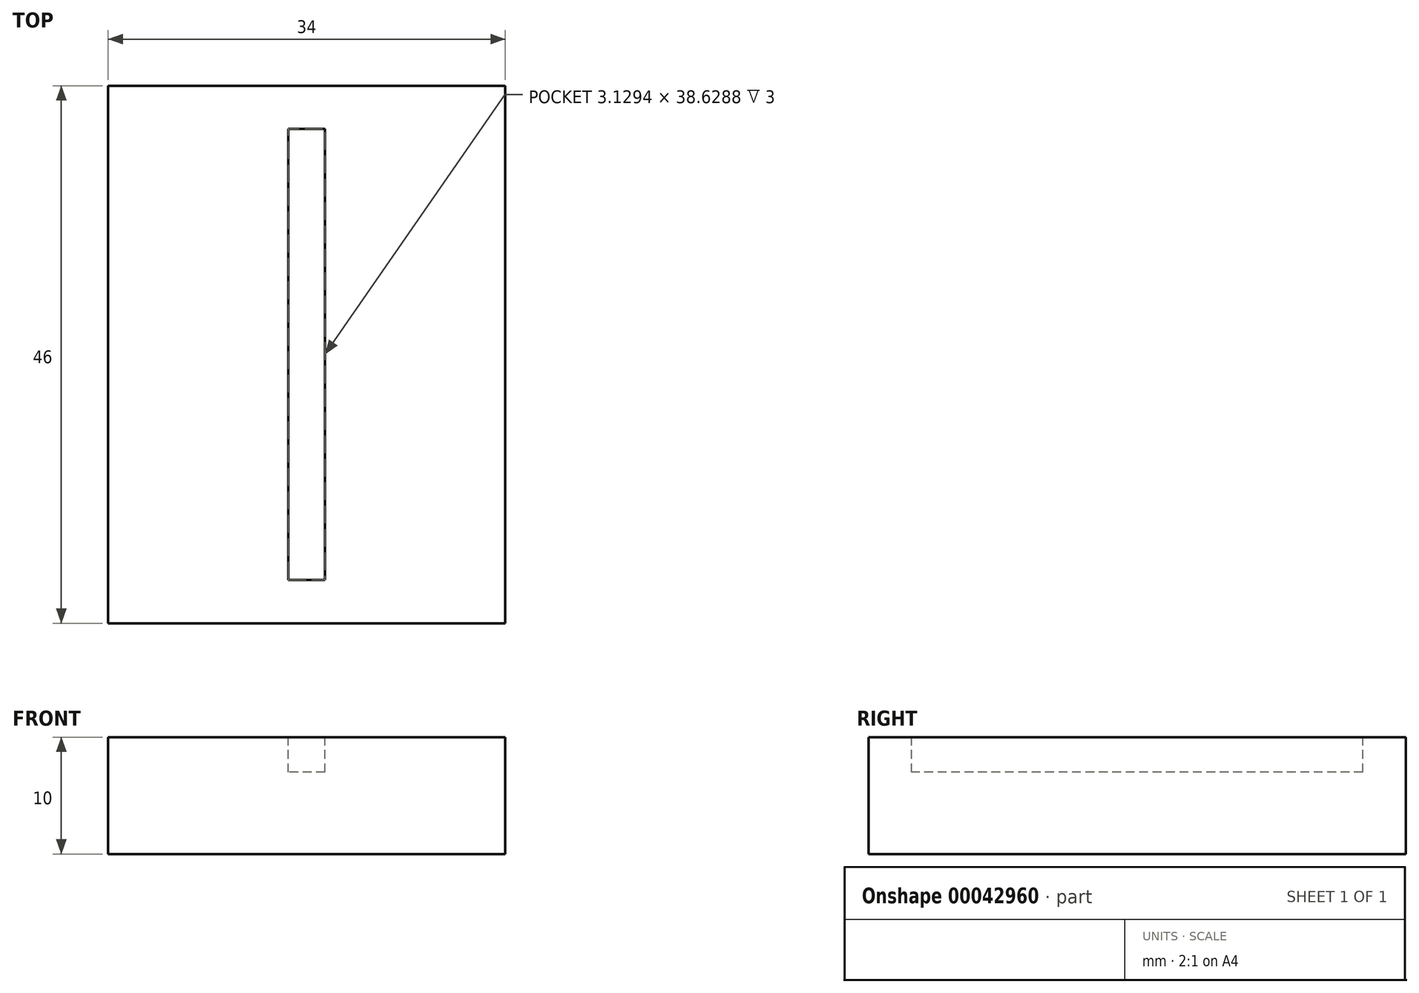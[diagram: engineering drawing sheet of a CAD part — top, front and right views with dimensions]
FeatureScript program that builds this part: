
annotation { "Feature Type Name" : "Feature", "Feature Type Description" : "" }
export const myFeature = defineFeature(function(context is Context, id is Id, definition is map)
    precondition{}
    {
        {
            var Q0;
            Q0=qCreatedBy(makeId("Top.planeOp"),FACE);
            var sketch = newSketch(context, id + "F0", { "sketchPlane" : qUnion([Q0])});
            skLineSegment(sketch, "E0.rect.bottom", {"start": v(17, 23) * mm, "end": v(-17, 23) * mm});
            skLineSegment(sketch, "E0.rect.top", {"start": v(17, -23) * mm, "end": v(-17, -23) * mm});
            skLineSegment(sketch, "E0.rect.left", {"start": v(17, 23) * mm, "end": v(17, -23) * mm});
            skLineSegment(sketch, "E0.rect.right", {"start": v(-17, 23) * mm, "end": v(-17, -23) * mm});
            skPoint(sketch, "E0.rect.middle", {"position": v(0, 0) * mm});
            skSolve(sketch);
        }
        {
            var Q0;
            Q0=makeQuery(id+"F0.imprint","IMPRINT",FACE,{"disambiguationData":[TD([[makeQuery(id+"F0.imprint","IMPRINT",EDGE,{"derivedFrom":sQuery(id+"F0.wireOp",EDGE,"E0.rect.bottom")}),1.0]])]});
            extrude(context, id + "F1", {"entities" : qUnion([Q0]), "depth" : 10 * mm});
        }
        {
            var Q0;
            Q0=makeQuery(id+"F1.opExtrude","CAP_FACE",FACE,{"disambiguationData":[OSD([sQuery(id+"F0.wireOp",EDGE,"E0.rect.bottom"),sQuery(id+"F0.wireOp",EDGE,"E0.rect.top"),sQuery(id+"F0.wireOp",EDGE,"E0.rect.left"),sQuery(id+"F0.wireOp",EDGE,"E0.rect.right")])],"isStart":false});
            var sketch = newSketch(context, id + "F2", { "sketchPlane" : qUnion([Q0])});
            skLineSegment(sketch, "E1.rect.bottom", {"start": v(1.56, 19.31) * mm, "end": v(-1.56, 19.31) * mm});
            skLineSegment(sketch, "E1.rect.top", {"start": v(1.56, -19.31) * mm, "end": v(-1.56, -19.31) * mm});
            skLineSegment(sketch, "E1.rect.left", {"start": v(1.56, 19.31) * mm, "end": v(1.56, -19.31) * mm});
            skLineSegment(sketch, "E1.rect.right", {"start": v(-1.56, 19.31) * mm, "end": v(-1.56, -19.31) * mm});
            skPoint(sketch, "E1.rect.middle", {"position": v(0, 0) * mm});
            skSolve(sketch);
        }
        {
            var Q0;
            Q0=makeQuery(id+"F2.imprint","IMPRINT",FACE,{"disambiguationData":[TD([[makeQuery(id+"F2.imprint","IMPRINT",EDGE,{"derivedFrom":sQuery(id+"F2.wireOp",EDGE,"E1.rect.bottom")}),1.0]])]});
            extrude(context, id + "F3", {"entities" : qUnion([Q0]), "operationType" : NewBodyOperationType.REMOVE, "oppositeDirection" : true, "depth" : 3 * mm});
        }
    });
